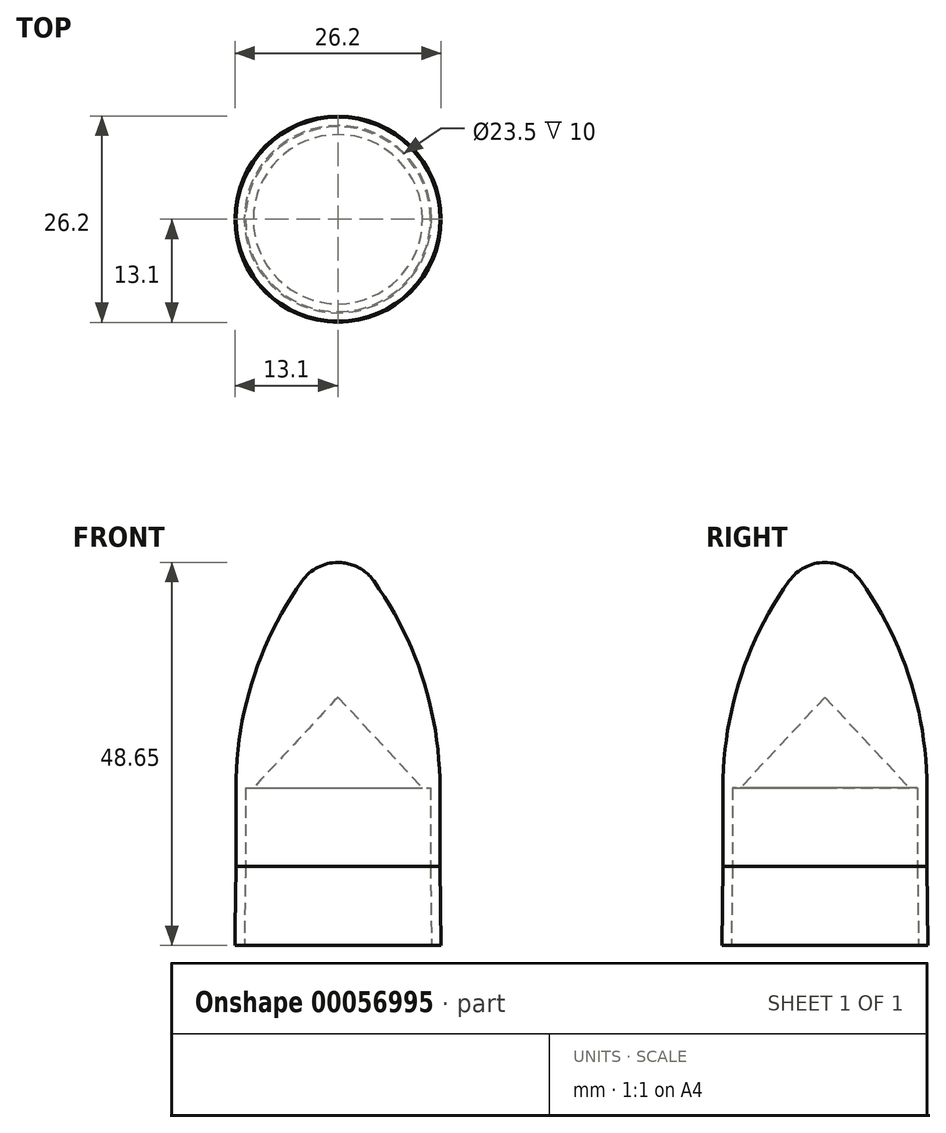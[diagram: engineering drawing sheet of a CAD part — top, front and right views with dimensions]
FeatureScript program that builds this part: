
annotation { "Feature Type Name" : "Feature", "Feature Type Description" : "" }
export const myFeature = defineFeature(function(context is Context, id is Id, definition is map)
    precondition{}
    {
        {
            var Q0;
            Q0=qCreatedBy(makeId("Front.planeOp"),FACE);
            var sketch = newSketch(context, id + "F0", { "sketchPlane" : qUnion([Q0])});
            skLineSegment(sketch, "E0", {"start": v(0, 0) * mm, "end": v(0, 50) * mm, "construction": true});
            skLineSegment(sketch, "E1", {"start": v(0, 0) * mm, "end": v(11.9, 0) * mm, "construction": true});
            skLineSegment(sketch, "E2", {"start": v(11.9, 0) * mm, "end": v(11.75, 10) * mm});
            skLineSegment(sketch, "E3", {"start": v(11.75, 10) * mm, "end": v(11.75, 20) * mm});
            skArc(sketch, "E4", {"start": v(11.75, 20) * mm, "mid": v(8.7, 36.1) * mm, "end": v(0, 50) * mm, "construction": true});
            skLineSegment(sketch, "E5", {"start": v(0, 50) * mm, "end": v(0, 31.53) * mm});
            skArc(sketch, "E6.0", {"start": v(12.95, 20) * mm, "mid": v(9.59, 37.14) * mm, "end": v(0, 51.74) * mm});
            skLineSegment(sketch, "E6.1", {"start": v(12.95, 10) * mm, "end": v(12.95, 20) * mm});
            skLineSegment(sketch, "E6.2", {"start": v(13.1, 0.03) * mm, "end": v(12.95, 10) * mm});
            skLineSegment(sketch, "E7", {"start": v(11.9, 0) * mm, "end": v(13.1, 0.03) * mm});
            skLineSegment(sketch, "E8", {"start": v(0, 50) * mm, "end": v(0, 51.74) * mm});
            skPoint(sketch, "E9.orphan", {"position": v(0, 51.74) * mm});
            skLineSegment(sketch, "E10", {"start": v(11.75, 20) * mm, "end": v(10.75, 20) * mm});
            skLineSegment(sketch, "E11", {"start": v(10.75, 20) * mm, "end": v(0, 31.53) * mm});
            skLineSegment(sketch, "E12", {"start": v(0, 86.72) * mm, "end": v(-0.39, 86.72) * mm, "construction": true});
            skLineSegment(sketch, "E13", {"start": v(0, 50) * mm, "end": v(-2.22, 50) * mm, "construction": true});
            skArc(sketch, "E14", {"start": v(4.55, 46.3) * mm, "mid": v(2.56, 48.02) * mm, "end": v(0, 48.65) * mm});
            skSolve(sketch);
        }
        {
            var Q0;
            Q0=makeQuery(id+"F0.imprint","IMPRINT",FACE,{"disambiguationData":[TD([[makeQuery(id+"F0.imprint","IMPRINT",EDGE,{"derivedFrom":sQuery(id+"F0.wireOp",EDGE,"E2")}),-1.0]])]});
            var Q1;
            Q1=sQuery(id+"F0.wireOp",EDGE,"E0");
            revolve(context, id + "F1", {"entities" : qUnion([Q0]), "axis" : qUnion([Q1]), "revolveType" : RevolveType.FULL});
        }
    });
